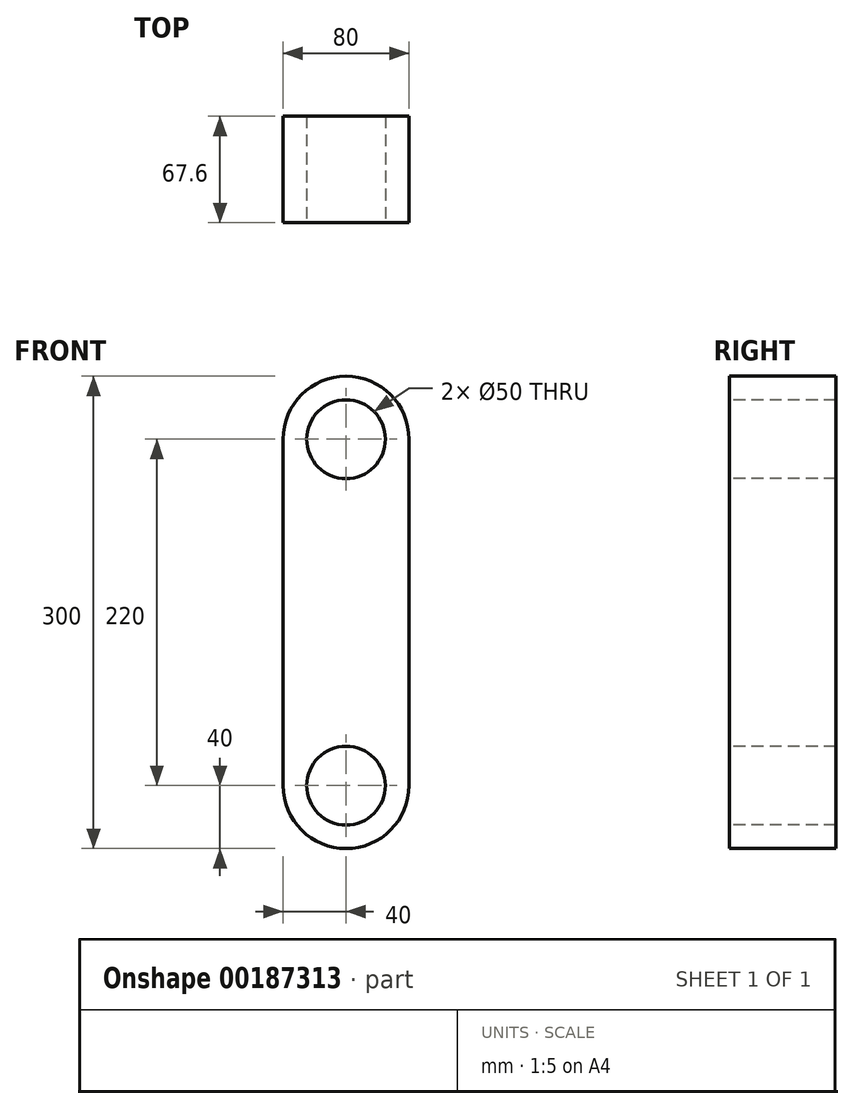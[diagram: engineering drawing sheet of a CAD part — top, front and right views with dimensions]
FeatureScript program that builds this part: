
annotation { "Feature Type Name" : "Feature", "Feature Type Description" : "" }
export const myFeature = defineFeature(function(context is Context, id is Id, definition is map)
    precondition{}
    {
        {
            var Q0;
            Q0=qCreatedBy(makeId("Front.planeOp"),FACE);
            var sketch = newSketch(context, id + "F0", { "sketchPlane" : qUnion([Q0])});
            skLineSegment(sketch, "E0.bottom", {"start": v(0, 150) * mm, "end": v(0, 150) * mm});
            skLineSegment(sketch, "E0.top", {"start": v(0, -150) * mm, "end": v(0, -150) * mm});
            skLineSegment(sketch, "E0.left", {"start": v(40, 110) * mm, "end": v(40, -110) * mm});
            skLineSegment(sketch, "E0.right", {"start": v(-40, 110) * mm, "end": v(-40, -110) * mm});
            skPoint(sketch, "E0.middle", {"position": v(0, 0) * mm});
            skPoint(sketch, "E1.visualSharp", {"position": v(-40, 150) * mm});
            skArc(sketch, "E1.filletArc", {"start": v(0, 150) * mm, "mid": v(-28.28, 138.28) * mm, "end": v(-40, 110) * mm});
            skPoint(sketch, "E2.visualSharp", {"position": v(40, 150) * mm});
            skArc(sketch, "E2.filletArc", {"start": v(40, 110) * mm, "mid": v(28.28, 138.28) * mm, "end": v(0, 150) * mm});
            skPoint(sketch, "E3.visualSharp", {"position": v(-40, -150) * mm});
            skArc(sketch, "E3.filletArc", {"start": v(-40, -110) * mm, "mid": v(-28.28, -138.28) * mm, "end": v(0, -150) * mm});
            skPoint(sketch, "E4.visualSharp", {"position": v(40, -150) * mm});
            skArc(sketch, "E4.filletArc", {"start": v(0, -150) * mm, "mid": v(28.28, -138.28) * mm, "end": v(40, -110) * mm});
            skSolve(sketch);
        }
        {
            var Q0;
            Q0=qSketchRegion(id+"F0",true);
            extrude(context, id + "F1", {"entities" : qUnion([Q0]), "depth" : 67.6 * mm});
        }
        {
            var Q0;
            Q0=makeQuery(id+"F1.opExtrude","CAP_FACE",FACE,{"disambiguationData":[OSD([sQuery(id+"F0.wireOp",EDGE,"E0.left"),sQuery(id+"F0.wireOp",EDGE,"E0.right"),sQuery(id+"F0.wireOp",EDGE,"E1.filletArc"),sQuery(id+"F0.wireOp",EDGE,"E2.filletArc"),sQuery(id+"F0.wireOp",EDGE,"E3.filletArc"),sQuery(id+"F0.wireOp",EDGE,"E4.filletArc")])],"isStart":false});
            var sketch = newSketch(context, id + "F2", { "sketchPlane" : qUnion([Q0])});
            skCircle(sketch, "E5", {"center": v(0, 110) * mm, "radius": 25 * mm});
            skCircle(sketch, "E6.MirrorC", {"center": v(0, -110) * mm, "radius": 25 * mm});
            skSolve(sketch);
        }
        {
            var Q0;
            Q0=qSketchRegion(id+"F2",true);
            var Q1;
            Q1=makeQuery(id+"F1.opExtrude","CAP_FACE",FACE,{"disambiguationData":[OSD([sQuery(id+"F0.wireOp",EDGE,"E0.left"),sQuery(id+"F0.wireOp",EDGE,"E0.right"),sQuery(id+"F0.wireOp",EDGE,"E1.filletArc"),sQuery(id+"F0.wireOp",EDGE,"E2.filletArc"),sQuery(id+"F0.wireOp",EDGE,"E3.filletArc"),sQuery(id+"F0.wireOp",EDGE,"E4.filletArc")])],"isStart":true});
            extrude(context, id + "F3", {"entities" : qUnion([Q0]), "operationType" : NewBodyOperationType.REMOVE, "endBound" : BoundingType.UP_TO_SURFACE, "oppositeDirection" : true, "endBoundEntityFace" : qUnion([Q1]), "depth" : 25 * mm});
        }
    });
